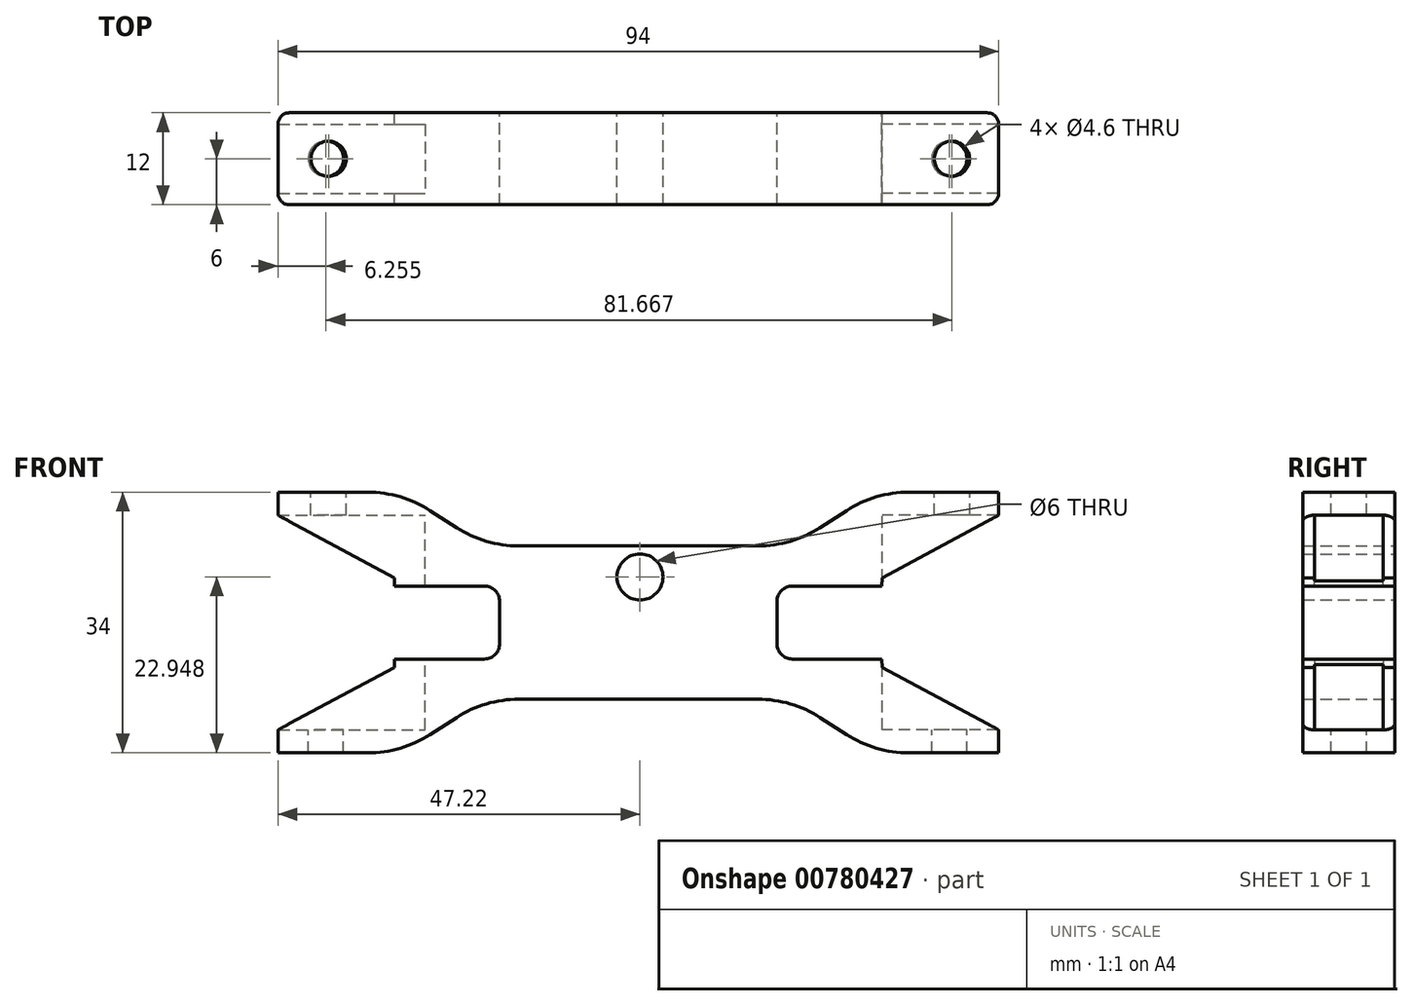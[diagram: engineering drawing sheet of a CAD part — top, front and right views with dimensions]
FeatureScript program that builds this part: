
annotation { "Feature Type Name" : "Feature", "Feature Type Description" : "" }
export const myFeature = defineFeature(function(context is Context, id is Id, definition is map)
    precondition{}
    {
        {
            var Q0;
            Q0=qCreatedBy(makeId("Front.planeOp"),FACE);
            var sketch = newSketch(context, id + "F0", { "sketchPlane" : qUnion([Q0])});
            skLineSegment(sketch, "E0.bottom", {"start": v(-31.1, 16.98) * mm, "end": v(-47.22, 16.98) * mm});
            skLineSegment(sketch, "E0.top", {"start": v(-0.22, -0.02) * mm, "end": v(-18.3, -0.02) * mm});
            skLineSegment(sketch, "E0.left", {"start": v(-0.22, 9.98) * mm, "end": v(-0.22, -0.02) * mm});
            skLineSegment(sketch, "E0.right", {"start": v(-47.22, 16.98) * mm, "end": v(-47.22, 13.98) * mm});
            skLineSegment(sketch, "E1.top", {"start": v(-0.22, 9.98) * mm, "end": v(-20.22, 9.98) * mm});
            skLineSegment(sketch, "E1.right", {"start": v(-31.1, 16.98) * mm, "end": v(-20.22, 9.98) * mm});
            skLineSegment(sketch, "E2.top", {"start": v(-32, 4.74) * mm, "end": v(-18.3, 4.74) * mm});
            skLineSegment(sketch, "E2.right", {"start": v(-18.3, -0.02) * mm, "end": v(-18.3, 4.74) * mm});
            skLineSegment(sketch, "E3.top", {"start": v(-47.22, 13.98) * mm, "end": v(-32.05, 5.82) * mm});
            skLineSegment(sketch, "E3.right", {"start": v(-32, 4.74) * mm, "end": v(-32.05, 5.82) * mm});
            skLineSegment(sketch, "E4.MirrorCS", {"start": v(-0.22, 9.98) * mm, "end": v(19.78, 9.98) * mm});
            skLineSegment(sketch, "E5.MirrorCS", {"start": v(30.66, 16.98) * mm, "end": v(19.78, 9.98) * mm});
            skLineSegment(sketch, "E6.MirrorCS", {"start": v(30.66, 16.98) * mm, "end": v(46.78, 16.98) * mm});
            skLineSegment(sketch, "E7.MirrorCS", {"start": v(46.78, 16.98) * mm, "end": v(46.78, 13.98) * mm});
            skLineSegment(sketch, "E8.MirrorCS", {"start": v(46.78, 13.98) * mm, "end": v(31.62, 5.82) * mm});
            skLineSegment(sketch, "E9.MirrorCS", {"start": v(31.57, 4.74) * mm, "end": v(31.62, 5.82) * mm});
            skLineSegment(sketch, "E10.MirrorCS", {"start": v(17.87, -0.02) * mm, "end": v(17.87, 4.74) * mm});
            skLineSegment(sketch, "E11.MirrorCS", {"start": v(-0.22, -0.02) * mm, "end": v(17.87, -0.02) * mm});
            skLineSegment(sketch, "E12.MirrorCS", {"start": v(31.57, 4.74) * mm, "end": v(17.87, 4.74) * mm});
            skLineSegment(sketch, "E13.MirrorCS", {"start": v(-0.22, -10.02) * mm, "end": v(-0.22, -0.02) * mm});
            skLineSegment(sketch, "E14.MirrorCS", {"start": v(-0.22, -10.02) * mm, "end": v(-20.22, -10.02) * mm});
            skLineSegment(sketch, "E15.MirrorCS", {"start": v(-31.1, -17.02) * mm, "end": v(-20.22, -10.02) * mm});
            skLineSegment(sketch, "E16.MirrorCS", {"start": v(-31.1, -17.02) * mm, "end": v(-47.22, -17.02) * mm});
            skLineSegment(sketch, "E17.MirrorCS", {"start": v(-47.22, -17.02) * mm, "end": v(-47.22, -14.02) * mm});
            skLineSegment(sketch, "E18.MirrorCS", {"start": v(-47.22, -14.02) * mm, "end": v(-32.05, -5.86) * mm});
            skLineSegment(sketch, "E19.MirrorCS", {"start": v(-32, -4.77) * mm, "end": v(-32.05, -5.86) * mm});
            skLineSegment(sketch, "E20.MirrorCS", {"start": v(-32, -4.77) * mm, "end": v(-18.3, -4.77) * mm});
            skLineSegment(sketch, "E21.MirrorCS", {"start": v(-18.3, -0.02) * mm, "end": v(-18.3, -4.77) * mm});
            skLineSegment(sketch, "E22.MirrorCS", {"start": v(17.87, -0.02) * mm, "end": v(17.87, -4.77) * mm});
            skLineSegment(sketch, "E23.MirrorCS", {"start": v(31.57, -4.77) * mm, "end": v(17.87, -4.77) * mm});
            skLineSegment(sketch, "E24.MirrorCS", {"start": v(31.57, -4.77) * mm, "end": v(31.62, -5.86) * mm});
            skLineSegment(sketch, "E25.MirrorCS", {"start": v(46.78, -14.02) * mm, "end": v(31.62, -5.86) * mm});
            skLineSegment(sketch, "E26.MirrorCS", {"start": v(46.78, -17.02) * mm, "end": v(46.78, -14.02) * mm});
            skLineSegment(sketch, "E27.MirrorCS", {"start": v(30.66, -17.02) * mm, "end": v(46.78, -17.02) * mm});
            skLineSegment(sketch, "E28.MirrorCS", {"start": v(30.66, -17.02) * mm, "end": v(19.78, -10.02) * mm});
            skLineSegment(sketch, "E29.MirrorCS", {"start": v(-0.22, -10.02) * mm, "end": v(19.78, -10.02) * mm});
            skSolve(sketch);
        }
        {
            var Q0;
            Q0=makeQuery(id+"F0.imprint","IMPRINT",FACE,{"disambiguationData":[TD([[makeQuery(id+"F0.imprint","IMPRINT",EDGE,{"derivedFrom":sQuery(id+"F0.wireOp",EDGE,"E11.MirrorCS")}),-1.0]])]});
            var Q1;
            Q1=makeQuery(id+"F0.imprint","IMPRINT",FACE,{"disambiguationData":[TD([[makeQuery(id+"F0.imprint","IMPRINT",EDGE,{"derivedFrom":sQuery(id+"F0.wireOp",EDGE,"E0.left")}),1.0]])]});
            var Q2;
            Q2=makeQuery(id+"F0.imprint","IMPRINT",FACE,{"disambiguationData":[TD([[makeQuery(id+"F0.imprint","IMPRINT",EDGE,{"derivedFrom":sQuery(id+"F0.wireOp",EDGE,"E0.top")}),1.0]])]});
            var Q3;
            Q3=makeQuery(id+"F0.imprint","IMPRINT",FACE,{"disambiguationData":[TD([[makeQuery(id+"F0.imprint","IMPRINT",EDGE,{"derivedFrom":sQuery(id+"F0.wireOp",EDGE,"E0.bottom")}),1.0]])]});
            extrude(context, id + "F1", {"entities" : qUnion([Q0, Q1, Q2, Q3]), "endBound" : BoundingType.SYMMETRIC, "depth" : 12 * mm, "offsetDistance" : 25 * mm});
        }
        {
            var Q0;
            Q0=qCreatedBy(makeId("Right.planeOp"),FACE);
            var sketch = newSketch(context, id + "F2", { "sketchPlane" : qUnion([Q0])});
            skLineSegment(sketch, "E30.bottom", {"start": v(0, 0) * mm, "end": v(4.5, 0) * mm});
            skLineSegment(sketch, "E30.top", {"start": v(0, 14) * mm, "end": v(4.5, 14) * mm});
            skLineSegment(sketch, "E30.left", {"start": v(0, 0) * mm, "end": v(0, 14) * mm});
            skLineSegment(sketch, "E30.right", {"start": v(4.5, 0) * mm, "end": v(4.5, 14) * mm});
            skLineSegment(sketch, "E31.MirrorCS", {"start": v(0, 14) * mm, "end": v(-4.5, 14) * mm});
            skLineSegment(sketch, "E32.MirrorCS", {"start": v(-4.5, 0) * mm, "end": v(-4.5, 14) * mm});
            skLineSegment(sketch, "E33.MirrorCS", {"start": v(0, 0) * mm, "end": v(-4.5, 0) * mm});
            skLineSegment(sketch, "E34.MirrorCS", {"start": v(4.5, 0) * mm, "end": v(4.5, -14) * mm});
            skLineSegment(sketch, "E35.MirrorCS", {"start": v(0, -14) * mm, "end": v(4.5, -14) * mm});
            skLineSegment(sketch, "E36.MirrorCS", {"start": v(0, 0) * mm, "end": v(0, -14) * mm});
            skLineSegment(sketch, "E37.MirrorCS", {"start": v(-4.5, 0) * mm, "end": v(-4.5, -14) * mm});
            skLineSegment(sketch, "E38.MirrorCS", {"start": v(0, -14) * mm, "end": v(-4.5, -14) * mm});
            skSolve(sketch);
        }
        {
            var Q0;
            Q0 = qSketchRegion(id + "F2", true);
            extrude(context, id + "F3", {"entities" : qUnion([Q0]), "depth" : 48.5 * mm, "offsetDistance" : 25 * mm});
        }
        {
            var Q0;
            Q0=makeQuery(id+"F3.opExtrude","SWEPT_BODY",BODY,{"disambiguationData":[OSD([sQuery(id+"F2.wireOp",EDGE,"E30.top"),sQuery(id+"F2.wireOp",EDGE,"E30.right"),sQuery(id+"F2.wireOp",EDGE,"E31.MirrorCS"),sQuery(id+"F2.wireOp",EDGE,"E32.MirrorCS"),sQuery(id+"F2.wireOp",EDGE,"E34.MirrorCS"),sQuery(id+"F2.wireOp",EDGE,"E35.MirrorCS"),sQuery(id+"F2.wireOp",EDGE,"E37.MirrorCS"),sQuery(id+"F2.wireOp",EDGE,"E38.MirrorCS")])]});
            var Q1;
            Q1=makeQuery(id+"F3.opExtrude","SWEPT_EDGE",EDGE,{"disambiguationData":[OSD([sQuery(id+"F2.wireOp",EDGE,"E31.MirrorCS"),sQuery(id+"F2.wireOp",EDGE,"E32.MirrorCS")])]});
            transform(context, id + "F4", {"entities" : qUnion([Q0]), "transformType" : TransformType.TRANSLATION_DISTANCE, "transformDirection" : qUnion([Q1]), "distance" : 31.6 * mm, "oppositeDirection" : true, "makeCopy" : false});
        }
        {
            var Q0;
            Q0=makeQuery(id+"F3.opExtrude","SWEPT_BODY",BODY,{"disambiguationData":[OSD([sQuery(id+"F2.wireOp",EDGE,"E30.top"),sQuery(id+"F2.wireOp",EDGE,"E30.right"),sQuery(id+"F2.wireOp",EDGE,"E31.MirrorCS"),sQuery(id+"F2.wireOp",EDGE,"E32.MirrorCS"),sQuery(id+"F2.wireOp",EDGE,"E34.MirrorCS"),sQuery(id+"F2.wireOp",EDGE,"E35.MirrorCS"),sQuery(id+"F2.wireOp",EDGE,"E37.MirrorCS"),sQuery(id+"F2.wireOp",EDGE,"E38.MirrorCS")])]});
            var Q1;
            Q1=makeQuery(id+"F1.opExtrude","SWEPT_FACE",FACE,{"disambiguationData":[OSD([sQuery(id+"F0.wireOp",EDGE,"E2.right"),sQuery(id+"F0.wireOp",EDGE,"E21.MirrorCS")])]});
            mirror(context, id + "F5", {"entities" : qUnion([Q0]), "mirrorPlane" : qUnion([Q1])});
        }
        {
            var Q0;
            Q0=makeQuery(id+"F5.opPattern","COPY",BODY,{"derivedFrom":makeQuery(id+"F3.opExtrude","SWEPT_BODY",BODY,{"disambiguationData":[OSD([sQuery(id+"F2.wireOp",EDGE,"E30.top"),sQuery(id+"F2.wireOp",EDGE,"E30.right"),sQuery(id+"F2.wireOp",EDGE,"E31.MirrorCS"),sQuery(id+"F2.wireOp",EDGE,"E32.MirrorCS"),sQuery(id+"F2.wireOp",EDGE,"E34.MirrorCS"),sQuery(id+"F2.wireOp",EDGE,"E35.MirrorCS"),sQuery(id+"F2.wireOp",EDGE,"E37.MirrorCS"),sQuery(id+"F2.wireOp",EDGE,"E38.MirrorCS")])]}),"instanceName":"1"});
            var Q1;
            Q1=makeQuery(id+"F5.opPattern","COPY",EDGE,{"derivedFrom":makeQuery(id+"F3.opExtrude","SWEPT_EDGE",EDGE,{"disambiguationData":[OSD([sQuery(id+"F2.wireOp",EDGE,"E30.top"),sQuery(id+"F2.wireOp",EDGE,"E30.right")])]}),"instanceName":"1"});
            var Q2;
            Q2=makeQuery(id+"F5.opPattern","COPY",EDGE,{"derivedFrom":makeQuery(id+"F3.opExtrude","SWEPT_EDGE",EDGE,{"disambiguationData":[OSD([sQuery(id+"F2.wireOp",EDGE,"E30.top"),sQuery(id+"F2.wireOp",EDGE,"E30.right")])]}),"instanceName":"1"});
            transform(context, id + "F6", {"entities" : qUnion([Q0]), "transformType" : TransformType.TRANSLATION_DISTANCE, "transformDirection" : qUnion([Q2]), "distance" : 40.2 * mm, "makeCopy" : false});
        }
        {
            var Q0;
            Q0=makeQuery(id+"F3.opExtrude","SWEPT_BODY",BODY,{"disambiguationData":[OSD([sQuery(id+"F2.wireOp",EDGE,"E30.top"),sQuery(id+"F2.wireOp",EDGE,"E30.right"),sQuery(id+"F2.wireOp",EDGE,"E31.MirrorCS"),sQuery(id+"F2.wireOp",EDGE,"E32.MirrorCS"),sQuery(id+"F2.wireOp",EDGE,"E34.MirrorCS"),sQuery(id+"F2.wireOp",EDGE,"E35.MirrorCS"),sQuery(id+"F2.wireOp",EDGE,"E37.MirrorCS"),sQuery(id+"F2.wireOp",EDGE,"E38.MirrorCS")])]});
            var Q1;
            Q1=makeQuery(id+"F1.opExtrude","SWEPT_BODY",BODY,{"disambiguationData":[OSD([sQuery(id+"F0.wireOp",EDGE,"E0.bottom"),sQuery(id+"F0.wireOp",EDGE,"E0.right"),sQuery(id+"F0.wireOp",EDGE,"E1.top"),sQuery(id+"F0.wireOp",EDGE,"E1.right"),sQuery(id+"F0.wireOp",EDGE,"E2.top"),sQuery(id+"F0.wireOp",EDGE,"E2.right"),sQuery(id+"F0.wireOp",EDGE,"E3.top"),sQuery(id+"F0.wireOp",EDGE,"E3.right"),sQuery(id+"F0.wireOp",EDGE,"E4.MirrorCS"),sQuery(id+"F0.wireOp",EDGE,"E5.MirrorCS"),sQuery(id+"F0.wireOp",EDGE,"E6.MirrorCS"),sQuery(id+"F0.wireOp",EDGE,"E7.MirrorCS"),sQuery(id+"F0.wireOp",EDGE,"E8.MirrorCS"),sQuery(id+"F0.wireOp",EDGE,"E9.MirrorCS"),sQuery(id+"F0.wireOp",EDGE,"E10.MirrorCS"),sQuery(id+"F0.wireOp",EDGE,"E12.MirrorCS"),sQuery(id+"F0.wireOp",EDGE,"E14.MirrorCS"),sQuery(id+"F0.wireOp",EDGE,"E15.MirrorCS"),sQuery(id+"F0.wireOp",EDGE,"E16.MirrorCS"),sQuery(id+"F0.wireOp",EDGE,"E17.MirrorCS"),sQuery(id+"F0.wireOp",EDGE,"E18.MirrorCS"),sQuery(id+"F0.wireOp",EDGE,"E19.MirrorCS"),sQuery(id+"F0.wireOp",EDGE,"E20.MirrorCS"),sQuery(id+"F0.wireOp",EDGE,"E21.MirrorCS"),sQuery(id+"F0.wireOp",EDGE,"E22.MirrorCS"),sQuery(id+"F0.wireOp",EDGE,"E23.MirrorCS"),sQuery(id+"F0.wireOp",EDGE,"E24.MirrorCS"),sQuery(id+"F0.wireOp",EDGE,"E25.MirrorCS"),sQuery(id+"F0.wireOp",EDGE,"E26.MirrorCS"),sQuery(id+"F0.wireOp",EDGE,"E27.MirrorCS"),sQuery(id+"F0.wireOp",EDGE,"E28.MirrorCS"),sQuery(id+"F0.wireOp",EDGE,"E29.MirrorCS")])]});
            booleanBodies(context, id + "F7", {"operationType" : BooleanOperationType.SUBTRACTION, "tools" : qUnion([Q0]), "targets" : qUnion([Q1])});
        }
        {
            var Q0;
            Q0=makeQuery(id+"F5.opPattern","COPY",BODY,{"derivedFrom":makeQuery(id+"F3.opExtrude","SWEPT_BODY",BODY,{"disambiguationData":[OSD([sQuery(id+"F2.wireOp",EDGE,"E30.top"),sQuery(id+"F2.wireOp",EDGE,"E30.right"),sQuery(id+"F2.wireOp",EDGE,"E31.MirrorCS"),sQuery(id+"F2.wireOp",EDGE,"E32.MirrorCS"),sQuery(id+"F2.wireOp",EDGE,"E34.MirrorCS"),sQuery(id+"F2.wireOp",EDGE,"E35.MirrorCS"),sQuery(id+"F2.wireOp",EDGE,"E37.MirrorCS"),sQuery(id+"F2.wireOp",EDGE,"E38.MirrorCS")])]}),"instanceName":"1"});
            var Q1;
            Q1=makeQuery(id+"F1.opExtrude","SWEPT_BODY",BODY,{"disambiguationData":[OSD([sQuery(id+"F0.wireOp",EDGE,"E0.bottom"),sQuery(id+"F0.wireOp",EDGE,"E0.right"),sQuery(id+"F0.wireOp",EDGE,"E1.top"),sQuery(id+"F0.wireOp",EDGE,"E1.right"),sQuery(id+"F0.wireOp",EDGE,"E2.top"),sQuery(id+"F0.wireOp",EDGE,"E2.right"),sQuery(id+"F0.wireOp",EDGE,"E3.top"),sQuery(id+"F0.wireOp",EDGE,"E3.right"),sQuery(id+"F0.wireOp",EDGE,"E4.MirrorCS"),sQuery(id+"F0.wireOp",EDGE,"E5.MirrorCS"),sQuery(id+"F0.wireOp",EDGE,"E6.MirrorCS"),sQuery(id+"F0.wireOp",EDGE,"E7.MirrorCS"),sQuery(id+"F0.wireOp",EDGE,"E8.MirrorCS"),sQuery(id+"F0.wireOp",EDGE,"E9.MirrorCS"),sQuery(id+"F0.wireOp",EDGE,"E10.MirrorCS"),sQuery(id+"F0.wireOp",EDGE,"E12.MirrorCS"),sQuery(id+"F0.wireOp",EDGE,"E14.MirrorCS"),sQuery(id+"F0.wireOp",EDGE,"E15.MirrorCS"),sQuery(id+"F0.wireOp",EDGE,"E16.MirrorCS"),sQuery(id+"F0.wireOp",EDGE,"E17.MirrorCS"),sQuery(id+"F0.wireOp",EDGE,"E18.MirrorCS"),sQuery(id+"F0.wireOp",EDGE,"E19.MirrorCS"),sQuery(id+"F0.wireOp",EDGE,"E20.MirrorCS"),sQuery(id+"F0.wireOp",EDGE,"E21.MirrorCS"),sQuery(id+"F0.wireOp",EDGE,"E22.MirrorCS"),sQuery(id+"F0.wireOp",EDGE,"E23.MirrorCS"),sQuery(id+"F0.wireOp",EDGE,"E24.MirrorCS"),sQuery(id+"F0.wireOp",EDGE,"E25.MirrorCS"),sQuery(id+"F0.wireOp",EDGE,"E26.MirrorCS"),sQuery(id+"F0.wireOp",EDGE,"E27.MirrorCS"),sQuery(id+"F0.wireOp",EDGE,"E28.MirrorCS"),sQuery(id+"F0.wireOp",EDGE,"E29.MirrorCS")])]});
            booleanBodies(context, id + "F8", {"operationType" : BooleanOperationType.SUBTRACTION, "tools" : qUnion([Q0]), "targets" : qUnion([Q1])});
        }
        {
            var Q0;
            Q0=qCreatedBy(makeId("Top.planeOp"),FACE);
            var sketch = newSketch(context, id + "F9", { "sketchPlane" : qUnion([Q0])});
            skLineSegment(sketch, "E39", {"start": v(-40.96, 0) * mm, "end": v(40.36, 0) * mm});
            skSolve(sketch);
        }
        {
            var Q0;
            Q0=sQuery(id+"F9.wireOp",VERTEX,"E39.start");
            var Q1;
            Q1=sQuery(id+"F9.wireOp",VERTEX,"E39.end");
            var Q2;
            Q2=makeQuery(id+"F1.opExtrude","SWEPT_BODY",BODY,{"disambiguationData":[OSD([sQuery(id+"F0.wireOp",EDGE,"E0.bottom"),sQuery(id+"F0.wireOp",EDGE,"E0.right"),sQuery(id+"F0.wireOp",EDGE,"E1.top"),sQuery(id+"F0.wireOp",EDGE,"E1.right"),sQuery(id+"F0.wireOp",EDGE,"E2.top"),sQuery(id+"F0.wireOp",EDGE,"E2.right"),sQuery(id+"F0.wireOp",EDGE,"E3.top"),sQuery(id+"F0.wireOp",EDGE,"E3.right"),sQuery(id+"F0.wireOp",EDGE,"E4.MirrorCS"),sQuery(id+"F0.wireOp",EDGE,"E5.MirrorCS"),sQuery(id+"F0.wireOp",EDGE,"E6.MirrorCS"),sQuery(id+"F0.wireOp",EDGE,"E7.MirrorCS"),sQuery(id+"F0.wireOp",EDGE,"E8.MirrorCS"),sQuery(id+"F0.wireOp",EDGE,"E9.MirrorCS"),sQuery(id+"F0.wireOp",EDGE,"E10.MirrorCS"),sQuery(id+"F0.wireOp",EDGE,"E12.MirrorCS"),sQuery(id+"F0.wireOp",EDGE,"E14.MirrorCS"),sQuery(id+"F0.wireOp",EDGE,"E15.MirrorCS"),sQuery(id+"F0.wireOp",EDGE,"E16.MirrorCS"),sQuery(id+"F0.wireOp",EDGE,"E17.MirrorCS"),sQuery(id+"F0.wireOp",EDGE,"E18.MirrorCS"),sQuery(id+"F0.wireOp",EDGE,"E19.MirrorCS"),sQuery(id+"F0.wireOp",EDGE,"E20.MirrorCS"),sQuery(id+"F0.wireOp",EDGE,"E21.MirrorCS"),sQuery(id+"F0.wireOp",EDGE,"E22.MirrorCS"),sQuery(id+"F0.wireOp",EDGE,"E23.MirrorCS"),sQuery(id+"F0.wireOp",EDGE,"E24.MirrorCS"),sQuery(id+"F0.wireOp",EDGE,"E25.MirrorCS"),sQuery(id+"F0.wireOp",EDGE,"E26.MirrorCS"),sQuery(id+"F0.wireOp",EDGE,"E27.MirrorCS"),sQuery(id+"F0.wireOp",EDGE,"E28.MirrorCS"),sQuery(id+"F0.wireOp",EDGE,"E29.MirrorCS")])]});
            hole(context, id + "F10", {"style" : HoleStyle.SIMPLE, "endStyle" : HoleEndStyle.BLIND, "holeDiameter" : 4.6 * mm, "majorDiameter" : 5 * mm, "holeDepth" : 5 * mm, "isTappedThrough" : true, "tappedDepth" : 12 * mm, "tapClearance" : 3, "locations" : qUnion([Q0, Q1]), "scope" : qUnion([Q2])});
        }
        {
            var Q0;
            Q0=makeQuery(id+"F1.opExtrude","CAP_EDGE",EDGE,{"disambiguationData":[OSD([sQuery(id+"F0.wireOp",EDGE,"E17.MirrorCS")])],"isStart":true});
            var Q1;
            Q1=makeQuery(id+"F1.opExtrude","CAP_EDGE",EDGE,{"disambiguationData":[OSD([sQuery(id+"F0.wireOp",EDGE,"E17.MirrorCS")])],"isStart":false});
            var Q2;
            Q2=makeQuery(id+"F1.opExtrude","CAP_EDGE",EDGE,{"disambiguationData":[OSD([sQuery(id+"F0.wireOp",EDGE,"E0.right")])],"isStart":false});
            var Q3;
            Q3=makeQuery(id+"F1.opExtrude","CAP_EDGE",EDGE,{"disambiguationData":[OSD([sQuery(id+"F0.wireOp",EDGE,"E0.right")])],"isStart":true});
            var Q4;
            Q4=makeQuery(id+"F1.opExtrude","CAP_EDGE",EDGE,{"disambiguationData":[OSD([sQuery(id+"F0.wireOp",EDGE,"E7.MirrorCS")])],"isStart":false});
            var Q5;
            Q5=makeQuery(id+"F1.opExtrude","CAP_EDGE",EDGE,{"disambiguationData":[OSD([sQuery(id+"F0.wireOp",EDGE,"E26.MirrorCS")])],"isStart":false});
            var Q6;
            Q6=makeQuery(id+"F1.opExtrude","CAP_EDGE",EDGE,{"disambiguationData":[OSD([sQuery(id+"F0.wireOp",EDGE,"E26.MirrorCS")])],"isStart":true});
            var Q7;
            Q7=makeQuery(id+"F1.opExtrude","CAP_EDGE",EDGE,{"disambiguationData":[OSD([sQuery(id+"F0.wireOp",EDGE,"E7.MirrorCS")])],"isStart":true});
            fillet(context, id + "F11", {"entities" : qUnion([Q0, Q1, Q2, Q3, Q4, Q5, Q6, Q7]), "radius" : 1.5 * mm, "tangentPropagation" : true, "allowEdgeOverflow" : false});
        }
        {
            var Q0;
            Q0=makeQuery(id+"F1.opExtrude","SWEPT_EDGE",EDGE,{"disambiguationData":[OSD([sQuery(id+"F0.wireOp",EDGE,"E0.bottom"),sQuery(id+"F0.wireOp",EDGE,"E1.right")])]});
            var Q1;
            Q1=makeQuery(id+"F1.opExtrude","SWEPT_EDGE",EDGE,{"disambiguationData":[OSD([sQuery(id+"F0.wireOp",EDGE,"E5.MirrorCS"),sQuery(id+"F0.wireOp",EDGE,"E6.MirrorCS")])]});
            var Q2;
            Q2=makeQuery(id+"F1.opExtrude","SWEPT_EDGE",EDGE,{"disambiguationData":[OSD([sQuery(id+"F0.wireOp",EDGE,"E27.MirrorCS"),sQuery(id+"F0.wireOp",EDGE,"E28.MirrorCS")])]});
            var Q3;
            Q3=makeQuery(id+"F1.opExtrude","SWEPT_EDGE",EDGE,{"disambiguationData":[OSD([sQuery(id+"F0.wireOp",EDGE,"E15.MirrorCS"),sQuery(id+"F0.wireOp",EDGE,"E16.MirrorCS")])]});
            var Q4;
            Q4=makeQuery(id+"F1.opExtrude","SWEPT_EDGE",EDGE,{"disambiguationData":[OSD([sQuery(id+"F0.wireOp",EDGE,"E28.MirrorCS"),sQuery(id+"F0.wireOp",EDGE,"E29.MirrorCS")])]});
            var Q5;
            Q5=makeQuery(id+"F1.opExtrude","SWEPT_EDGE",EDGE,{"disambiguationData":[OSD([sQuery(id+"F0.wireOp",EDGE,"E14.MirrorCS"),sQuery(id+"F0.wireOp",EDGE,"E15.MirrorCS")])]});
            var Q6;
            Q6=makeQuery(id+"F1.opExtrude","SWEPT_EDGE",EDGE,{"disambiguationData":[OSD([sQuery(id+"F0.wireOp",EDGE,"E4.MirrorCS"),sQuery(id+"F0.wireOp",EDGE,"E5.MirrorCS")])]});
            var Q7;
            Q7=makeQuery(id+"F1.opExtrude","SWEPT_EDGE",EDGE,{"disambiguationData":[OSD([sQuery(id+"F0.wireOp",EDGE,"E1.top"),sQuery(id+"F0.wireOp",EDGE,"E1.right")])]});
            fillet(context, id + "F12", {"entities" : qUnion([Q0, Q1, Q2, Q3, Q4, Q5, Q6, Q7]), "radius" : 15 * mm, "tangentPropagation" : true, "allowEdgeOverflow" : false});
        }
        {
            var Q0;
            Q0=makeQuery(id+"F1.opExtrude","SWEPT_FACE",FACE,{"disambiguationData":[OSD([sQuery(id+"F0.wireOp",EDGE,"E0.bottom")])]});
            var sketch = newSketch(context, id + "F13", { "sketchPlane" : qUnion([Q0])});
            skLineSegment(sketch, "E40", {"start": v(-40.62, 0) * mm, "end": v(40.7, 0) * mm});
            skSolve(sketch);
        }
        {
            var Q0;
            Q0=sQuery(id+"F13.wireOp",VERTEX,"E40.start");
            var Q1;
            Q1=sQuery(id+"F13.wireOp",VERTEX,"E40.end");
            var Q2;
            Q2=makeQuery(id+"F1.opExtrude","SWEPT_BODY",BODY,{"disambiguationData":[OSD([sQuery(id+"F0.wireOp",EDGE,"E0.bottom"),sQuery(id+"F0.wireOp",EDGE,"E0.right"),sQuery(id+"F0.wireOp",EDGE,"E1.top"),sQuery(id+"F0.wireOp",EDGE,"E1.right"),sQuery(id+"F0.wireOp",EDGE,"E2.top"),sQuery(id+"F0.wireOp",EDGE,"E2.right"),sQuery(id+"F0.wireOp",EDGE,"E3.top"),sQuery(id+"F0.wireOp",EDGE,"E3.right"),sQuery(id+"F0.wireOp",EDGE,"E4.MirrorCS"),sQuery(id+"F0.wireOp",EDGE,"E5.MirrorCS"),sQuery(id+"F0.wireOp",EDGE,"E6.MirrorCS"),sQuery(id+"F0.wireOp",EDGE,"E7.MirrorCS"),sQuery(id+"F0.wireOp",EDGE,"E8.MirrorCS"),sQuery(id+"F0.wireOp",EDGE,"E9.MirrorCS"),sQuery(id+"F0.wireOp",EDGE,"E10.MirrorCS"),sQuery(id+"F0.wireOp",EDGE,"E12.MirrorCS"),sQuery(id+"F0.wireOp",EDGE,"E14.MirrorCS"),sQuery(id+"F0.wireOp",EDGE,"E15.MirrorCS"),sQuery(id+"F0.wireOp",EDGE,"E16.MirrorCS"),sQuery(id+"F0.wireOp",EDGE,"E17.MirrorCS"),sQuery(id+"F0.wireOp",EDGE,"E18.MirrorCS"),sQuery(id+"F0.wireOp",EDGE,"E19.MirrorCS"),sQuery(id+"F0.wireOp",EDGE,"E20.MirrorCS"),sQuery(id+"F0.wireOp",EDGE,"E21.MirrorCS"),sQuery(id+"F0.wireOp",EDGE,"E22.MirrorCS"),sQuery(id+"F0.wireOp",EDGE,"E23.MirrorCS"),sQuery(id+"F0.wireOp",EDGE,"E24.MirrorCS"),sQuery(id+"F0.wireOp",EDGE,"E25.MirrorCS"),sQuery(id+"F0.wireOp",EDGE,"E26.MirrorCS"),sQuery(id+"F0.wireOp",EDGE,"E27.MirrorCS"),sQuery(id+"F0.wireOp",EDGE,"E28.MirrorCS"),sQuery(id+"F0.wireOp",EDGE,"E29.MirrorCS")])]});
            hole(context, id + "F14", {"style" : HoleStyle.SIMPLE, "endStyle" : HoleEndStyle.BLIND, "holeDiameter" : 4.6 * mm, "majorDiameter" : 5 * mm, "holeDepth" : 5 * mm, "isTappedThrough" : true, "tappedDepth" : 12 * mm, "tapClearance" : 3, "locations" : qUnion([Q0, Q1]), "scope" : qUnion([Q2])});
        }
        {
            var Q0;
            Q0=makeQuery(id+"F1.opExtrude","CAP_FACE",FACE,{"disambiguationData":[OSD([sQuery(id+"F0.wireOp",EDGE,"E0.bottom"),sQuery(id+"F0.wireOp",EDGE,"E0.right"),sQuery(id+"F0.wireOp",EDGE,"E1.top"),sQuery(id+"F0.wireOp",EDGE,"E1.right"),sQuery(id+"F0.wireOp",EDGE,"E2.top"),sQuery(id+"F0.wireOp",EDGE,"E2.right"),sQuery(id+"F0.wireOp",EDGE,"E3.top"),sQuery(id+"F0.wireOp",EDGE,"E3.right"),sQuery(id+"F0.wireOp",EDGE,"E4.MirrorCS"),sQuery(id+"F0.wireOp",EDGE,"E5.MirrorCS"),sQuery(id+"F0.wireOp",EDGE,"E6.MirrorCS"),sQuery(id+"F0.wireOp",EDGE,"E7.MirrorCS"),sQuery(id+"F0.wireOp",EDGE,"E8.MirrorCS"),sQuery(id+"F0.wireOp",EDGE,"E9.MirrorCS"),sQuery(id+"F0.wireOp",EDGE,"E10.MirrorCS"),sQuery(id+"F0.wireOp",EDGE,"E12.MirrorCS"),sQuery(id+"F0.wireOp",EDGE,"E14.MirrorCS"),sQuery(id+"F0.wireOp",EDGE,"E15.MirrorCS"),sQuery(id+"F0.wireOp",EDGE,"E16.MirrorCS"),sQuery(id+"F0.wireOp",EDGE,"E17.MirrorCS"),sQuery(id+"F0.wireOp",EDGE,"E18.MirrorCS"),sQuery(id+"F0.wireOp",EDGE,"E19.MirrorCS"),sQuery(id+"F0.wireOp",EDGE,"E20.MirrorCS"),sQuery(id+"F0.wireOp",EDGE,"E21.MirrorCS"),sQuery(id+"F0.wireOp",EDGE,"E22.MirrorCS"),sQuery(id+"F0.wireOp",EDGE,"E23.MirrorCS"),sQuery(id+"F0.wireOp",EDGE,"E24.MirrorCS"),sQuery(id+"F0.wireOp",EDGE,"E25.MirrorCS"),sQuery(id+"F0.wireOp",EDGE,"E26.MirrorCS"),sQuery(id+"F0.wireOp",EDGE,"E27.MirrorCS"),sQuery(id+"F0.wireOp",EDGE,"E28.MirrorCS"),sQuery(id+"F0.wireOp",EDGE,"E29.MirrorCS")])],"isStart":true});
            var sketch = newSketch(context, id + "F15", { "sketchPlane" : qUnion([Q0])});
            skLineSegment(sketch, "E41", {"start": v(0.22, 9.98) * mm, "end": v(0, 5.93) * mm});
            skSolve(sketch);
        }
        {
            var Q0;
            Q0=sQuery(id+"F15.wireOp",VERTEX,"E41.end");
            var Q1;
            Q1=makeQuery(id+"F1.opExtrude","SWEPT_BODY",BODY,{"disambiguationData":[OSD([sQuery(id+"F0.wireOp",EDGE,"E0.bottom"),sQuery(id+"F0.wireOp",EDGE,"E0.right"),sQuery(id+"F0.wireOp",EDGE,"E1.top"),sQuery(id+"F0.wireOp",EDGE,"E1.right"),sQuery(id+"F0.wireOp",EDGE,"E2.top"),sQuery(id+"F0.wireOp",EDGE,"E2.right"),sQuery(id+"F0.wireOp",EDGE,"E3.top"),sQuery(id+"F0.wireOp",EDGE,"E3.right"),sQuery(id+"F0.wireOp",EDGE,"E4.MirrorCS"),sQuery(id+"F0.wireOp",EDGE,"E5.MirrorCS"),sQuery(id+"F0.wireOp",EDGE,"E6.MirrorCS"),sQuery(id+"F0.wireOp",EDGE,"E7.MirrorCS"),sQuery(id+"F0.wireOp",EDGE,"E8.MirrorCS"),sQuery(id+"F0.wireOp",EDGE,"E9.MirrorCS"),sQuery(id+"F0.wireOp",EDGE,"E10.MirrorCS"),sQuery(id+"F0.wireOp",EDGE,"E12.MirrorCS"),sQuery(id+"F0.wireOp",EDGE,"E14.MirrorCS"),sQuery(id+"F0.wireOp",EDGE,"E15.MirrorCS"),sQuery(id+"F0.wireOp",EDGE,"E16.MirrorCS"),sQuery(id+"F0.wireOp",EDGE,"E17.MirrorCS"),sQuery(id+"F0.wireOp",EDGE,"E18.MirrorCS"),sQuery(id+"F0.wireOp",EDGE,"E19.MirrorCS"),sQuery(id+"F0.wireOp",EDGE,"E20.MirrorCS"),sQuery(id+"F0.wireOp",EDGE,"E21.MirrorCS"),sQuery(id+"F0.wireOp",EDGE,"E22.MirrorCS"),sQuery(id+"F0.wireOp",EDGE,"E23.MirrorCS"),sQuery(id+"F0.wireOp",EDGE,"E24.MirrorCS"),sQuery(id+"F0.wireOp",EDGE,"E25.MirrorCS"),sQuery(id+"F0.wireOp",EDGE,"E26.MirrorCS"),sQuery(id+"F0.wireOp",EDGE,"E27.MirrorCS"),sQuery(id+"F0.wireOp",EDGE,"E28.MirrorCS"),sQuery(id+"F0.wireOp",EDGE,"E29.MirrorCS")])]});
            hole(context, id + "F16", {"style" : HoleStyle.SIMPLE, "endStyle" : HoleEndStyle.BLIND, "holeDiameter" : 6 * mm, "majorDiameter" : 5 * mm, "holeDepth" : 25 * mm, "isTappedThrough" : true, "tappedDepth" : 12 * mm, "tapClearance" : 3, "locations" : qUnion([Q0]), "scope" : qUnion([Q1])});
        }
        {
            var Q0;
            Q0=makeQuery(id+"F1.opExtrude","SWEPT_EDGE",EDGE,{"disambiguationData":[OSD([sQuery(id+"F0.wireOp",EDGE,"E10.MirrorCS"),sQuery(id+"F0.wireOp",EDGE,"E12.MirrorCS")])]});
            var Q1;
            Q1=makeQuery(id+"F1.opExtrude","SWEPT_EDGE",EDGE,{"disambiguationData":[OSD([sQuery(id+"F0.wireOp",EDGE,"E2.top"),sQuery(id+"F0.wireOp",EDGE,"E2.right")])]});
            var Q2;
            Q2=makeQuery(id+"F1.opExtrude","SWEPT_EDGE",EDGE,{"disambiguationData":[OSD([sQuery(id+"F0.wireOp",EDGE,"E20.MirrorCS"),sQuery(id+"F0.wireOp",EDGE,"E21.MirrorCS")])]});
            var Q3;
            Q3=makeQuery(id+"F1.opExtrude","SWEPT_EDGE",EDGE,{"disambiguationData":[OSD([sQuery(id+"F0.wireOp",EDGE,"E22.MirrorCS"),sQuery(id+"F0.wireOp",EDGE,"E23.MirrorCS")])]});
            fillet(context, id + "F17", {"entities" : qUnion([Q0, Q1, Q2, Q3]), "radius" : 2 * mm, "tangentPropagation" : true, "allowEdgeOverflow" : false});
        }
    });
